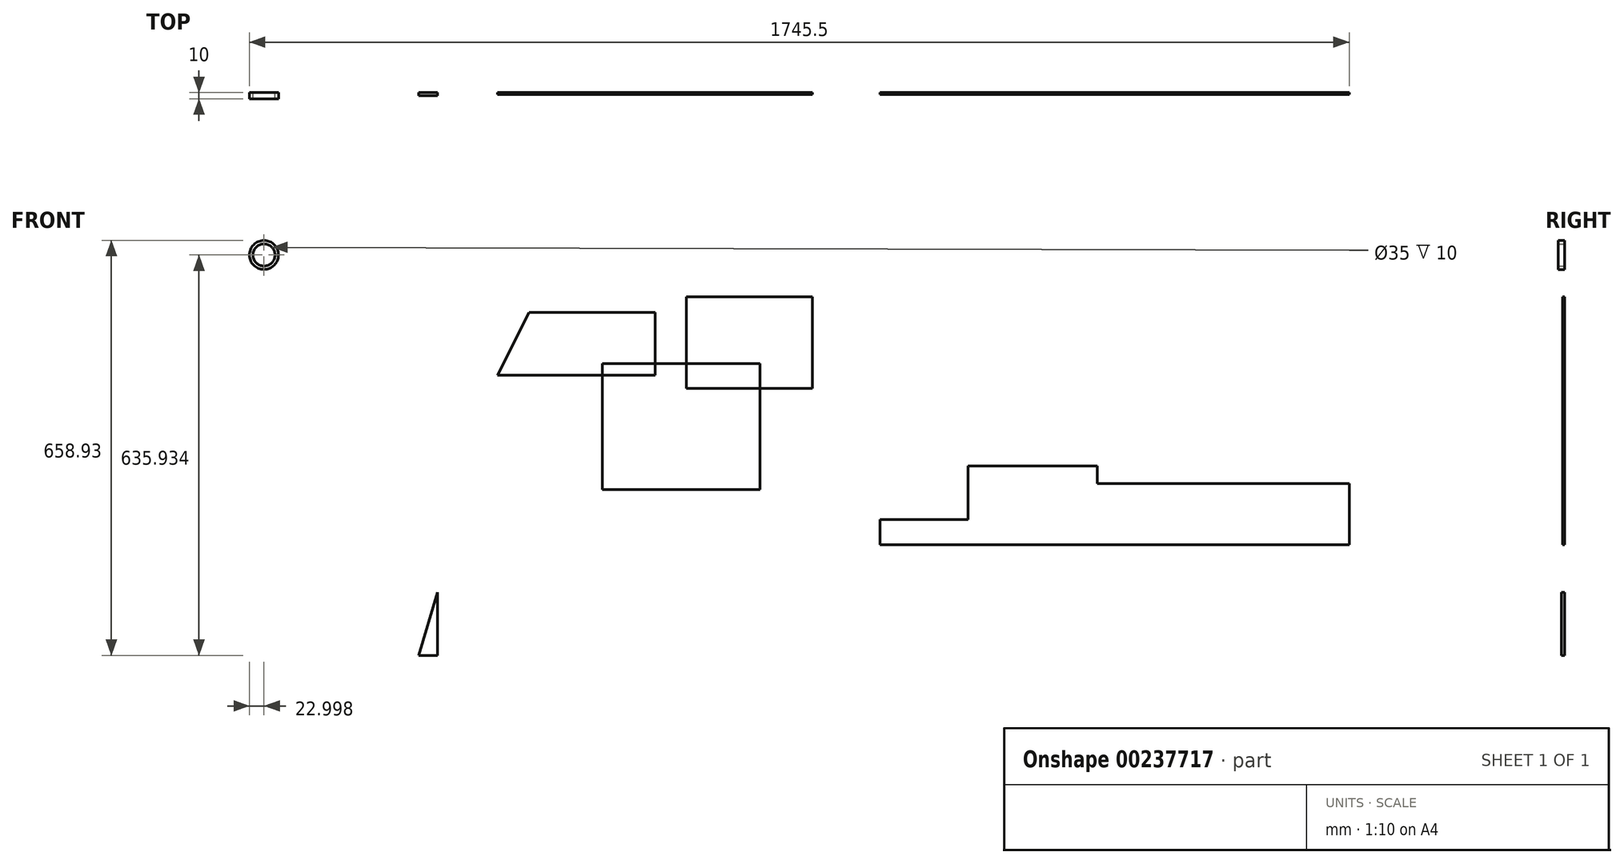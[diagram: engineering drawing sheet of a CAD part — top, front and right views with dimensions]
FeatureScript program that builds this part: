
annotation { "Feature Type Name" : "Feature", "Feature Type Description" : "" }
export const myFeature = defineFeature(function(context is Context, id is Id, definition is map)
    precondition{}
    {
        {
            var Q0;
            Q0=qCreatedBy(makeId("Front.planeOp"),FACE);
            var sketch = newSketch(context, id + "F0", { "sketchPlane" : qUnion([Q0])});
            skLineSegment(sketch, "E0.bottom", {"start": v(0, 124.32) * mm, "end": v(200, 124.32) * mm});
            skLineSegment(sketch, "E0.top", {"start": v(0, -20.68) * mm, "end": v(200, -20.68) * mm});
            skLineSegment(sketch, "E0.left", {"start": v(0, 124.32) * mm, "end": v(0, -20.68) * mm});
            skLineSegment(sketch, "E0.right", {"start": v(200, 124.32) * mm, "end": v(200, -20.68) * mm});
            skSolve(sketch);
        }
        {
            var Q0;
            Q0=makeQuery(id+"F0.imprint","IMPRINT",FACE,{"disambiguationData":[TD([[makeQuery(id+"F0.imprint","IMPRINT",EDGE,{"derivedFrom":sQuery(id+"F0.wireOp",EDGE,"E0.bottom")}),-1.0]])]});
            extrude(context, id + "F1", {"entities" : qUnion([Q0]), "depth" : 3 * mm});
        }
        {
            var Q0;
            Q0=qCreatedBy(makeId("Front.planeOp"),FACE);
            var sketch = newSketch(context, id + "F2", { "sketchPlane" : qUnion([Q0])});
            skLineSegment(sketch, "E1.bottom", {"start": v(-50, 0) * mm, "end": v(-300, 0) * mm});
            skLineSegment(sketch, "E1.left", {"start": v(-50, 0) * mm, "end": v(-50, 100) * mm});
            skLineSegment(sketch, "E2", {"start": v(-50, 100) * mm, "end": v(-250, 100) * mm});
            skLineSegment(sketch, "E3", {"start": v(-250, 100) * mm, "end": v(-300, 0) * mm});
            skSolve(sketch);
        }
        {
            var Q0;
            Q0=makeQuery(id+"F2.imprint","IMPRINT",FACE,{"disambiguationData":[TD([[makeQuery(id+"F2.imprint","IMPRINT",EDGE,{"derivedFrom":sQuery(id+"F2.wireOp",EDGE,"E1.bottom")}),-1.0]])]});
            extrude(context, id + "F3", {"entities" : qUnion([Q0]), "depth" : 3 * mm});
        }
        {
            var Q0;
            Q0=qCreatedBy(makeId("Front.planeOp"),FACE);
            var sketch = newSketch(context, id + "F4", { "sketchPlane" : qUnion([Q0])});
            skLineSegment(sketch, "E4.bottom", {"start": v(-133.42, 18.3) * mm, "end": v(116.58, 18.3) * mm});
            skLineSegment(sketch, "E4.top", {"start": v(-133.42, -181.7) * mm, "end": v(116.58, -181.7) * mm});
            skLineSegment(sketch, "E4.left", {"start": v(-133.42, 18.3) * mm, "end": v(-133.42, -181.7) * mm});
            skLineSegment(sketch, "E4.right", {"start": v(116.58, 18.3) * mm, "end": v(116.58, -181.7) * mm});
            skSolve(sketch);
        }
        {
            var Q0;
            Q0=makeQuery(id+"F4.imprint","IMPRINT",FACE,{"disambiguationData":[TD([[makeQuery(id+"F4.imprint","IMPRINT",EDGE,{"derivedFrom":sQuery(id+"F4.wireOp",EDGE,"E4.bottom")}),-1.0]])]});
            extrude(context, id + "F5", {"entities" : qUnion([Q0]), "depth" : 3 * mm});
        }
        {
            var Q0;
            Q0=qCreatedBy(makeId("Front.planeOp"),FACE);
            var sketch = newSketch(context, id + "F6", { "sketchPlane" : qUnion([Q0])});
            skLineSegment(sketch, "E5.bottom", {"start": v(446.86, -144.17) * mm, "end": v(651.86, -144.17) * mm});
            skLineSegment(sketch, "E5.top", {"start": v(306.86, -269.17) * mm, "end": v(1051.86, -269.17) * mm});
            skLineSegment(sketch, "E5.left", {"start": v(306.86, -229.17) * mm, "end": v(306.86, -269.17) * mm});
            skLineSegment(sketch, "E5.right", {"start": v(1051.86, -171.75) * mm, "end": v(1051.86, -269.17) * mm});
            skLineSegment(sketch, "E6", {"start": v(306.86, -229.17) * mm, "end": v(446.86, -229.17) * mm});
            skLineSegment(sketch, "E7", {"start": v(446.86, -229.17) * mm, "end": v(446.86, -144.17) * mm});
            skLineSegment(sketch, "E8", {"start": v(1051.86, -171.75) * mm, "end": v(651.86, -171.75) * mm});
            skLineSegment(sketch, "E9", {"start": v(651.86, -171.75) * mm, "end": v(651.86, -144.17) * mm});
            skPoint(sketch, "E10.orphan", {"position": v(446.86, -269.17) * mm});
            skSolve(sketch);
        }
        {
            var Q0;
            Q0=makeQuery(id+"F6.imprint","IMPRINT",FACE,{"disambiguationData":[TD([[makeQuery(id+"F6.imprint","IMPRINT",EDGE,{"derivedFrom":sQuery(id+"F6.wireOp",EDGE,"E5.bottom")}),-1.0]])]});
            extrude(context, id + "F7", {"entities" : qUnion([Q0]), "depth" : 3 * mm});
        }
        {
            var Q0;
            Q0=qCreatedBy(makeId("Front.planeOp"),FACE);
            var sketch = newSketch(context, id + "F8", { "sketchPlane" : qUnion([Q0])});
            skLineSegment(sketch, "E11", {"start": v(-425.38, -444.92) * mm, "end": v(-395.38, -444.92) * mm});
            skLineSegment(sketch, "E12", {"start": v(-395.38, -444.92) * mm, "end": v(-395.38, -344.92) * mm});
            skLineSegment(sketch, "E13", {"start": v(-395.38, -344.92) * mm, "end": v(-425.38, -444.92) * mm});
            skSolve(sketch);
        }
        {
            var Q0;
            Q0=makeQuery(id+"F8.imprint","IMPRINT",FACE,{"disambiguationData":[TD([[makeQuery(id+"F8.imprint","IMPRINT",EDGE,{"derivedFrom":sQuery(id+"F8.wireOp",EDGE,"E11")}),1.0]])]});
            extrude(context, id + "F9", {"entities" : qUnion([Q0]), "depth" : 5 * mm});
        }
        {
            var Q0;
            Q0=qCreatedBy(makeId("Front.planeOp"),FACE);
            var sketch = newSketch(context, id + "F10", { "sketchPlane" : qUnion([Q0])});
            skCircle(sketch, "E14", {"center": v(-670.64, 191.01) * mm, "radius": 17.5 * mm});
            skCircle(sketch, "E15", {"center": v(-670.64, 191.01) * mm, "radius": 23 * mm});
            skSolve(sketch);
        }
        {
            var Q0;
            Q0=makeQuery(id+"F10.imprint","IMPRINT",FACE,{"disambiguationData":[TD([[makeQuery(id+"F10.imprint","IMPRINT",EDGE,{"derivedFrom":sQuery(id+"F10.wireOp",EDGE,"E14")}),-1.0]])]});
            extrude(context, id + "F11", {"entities" : qUnion([Q0]), "depth" : 10 * mm});
        }
    });
